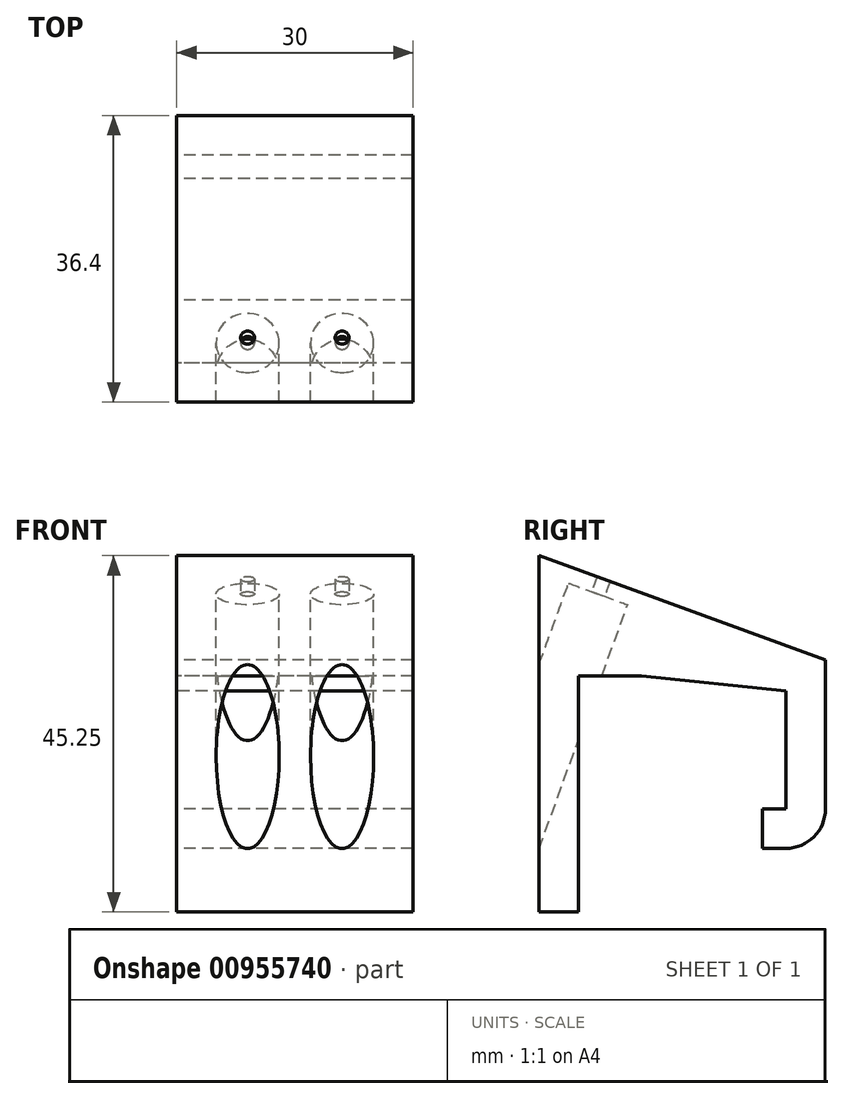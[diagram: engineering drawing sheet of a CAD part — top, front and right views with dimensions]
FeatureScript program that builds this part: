
annotation { "Feature Type Name" : "Feature", "Feature Type Description" : "" }
export const myFeature = defineFeature(function(context is Context, id is Id, definition is map)
    precondition{}
    {
        {
            var Q0;
            Q0=qCreatedBy(makeId("Right.planeOp"),FACE);
            var sketch = newSketch(context, id + "F0", { "sketchPlane" : qUnion([Q0])});
            skLineSegment(sketch, "E0", {"start": v(-5, -30) * mm, "end": v(-5, 15.25) * mm});
            skLineSegment(sketch, "E1", {"start": v(-5, 15.25) * mm, "end": v(31.4, 2) * mm});
            skLineSegment(sketch, "E2", {"start": v(31.4, 2) * mm, "end": v(31.4, -21.93) * mm});
            skLineSegment(sketch, "E3", {"start": v(31.4, -21.93) * mm, "end": v(23.4, -21.93) * mm});
            skLineSegment(sketch, "E4", {"start": v(23.4, -21.93) * mm, "end": v(23.4, -16.93) * mm});
            skLineSegment(sketch, "E5", {"start": v(23.4, -16.93) * mm, "end": v(26.4, -16.93) * mm});
            skLineSegment(sketch, "E6", {"start": v(26.4, -16.93) * mm, "end": v(26.4, -1.93) * mm});
            skLineSegment(sketch, "E7", {"start": v(26.4, -1.93) * mm, "end": v(8, 0) * mm});
            skLineSegment(sketch, "E8", {"start": v(8, 0) * mm, "end": v(0, 0) * mm});
            skLineSegment(sketch, "E9", {"start": v(0, 0) * mm, "end": v(0, -30) * mm});
            skLineSegment(sketch, "E10", {"start": v(0, -30) * mm, "end": v(-5, -30) * mm});
            skSolve(sketch);
        }
        {
            var Q0;
            Q0=makeQuery(id+"F0.imprint","IMPRINT",FACE,{"disambiguationData":[TD([[makeQuery(id+"F0.imprint","IMPRINT",EDGE,{"derivedFrom":sQuery(id+"F0.wireOp",EDGE,"E0")}),-1.0]])]});
            extrude(context, id + "F1", {"entities" : qUnion([Q0]), "depth" : 30 * mm, "offsetDistance" : 25 * mm, "symmetric" : true});
        }
        {
            var Q0;
            Q0=makeQuery(id+"F1.opExtrude","SWEPT_FACE",FACE,{"disambiguationData":[OSD([sQuery(id+"F0.wireOp",EDGE,"E1")])]});
            var sketch = newSketch(context, id + "F2", { "sketchPlane" : qUnion([Q0])});
            skCircle(sketch, "E11", {"center": v(-6, -1.18) * mm, "radius": 4 * mm});
            skCircle(sketch, "E12", {"center": v(6, -1.18) * mm, "radius": 4 * mm});
            skSolve(sketch);
        }
        {
            var Q0;
            Q0=makeQuery(id+"F2.imprint","IMPRINT",FACE,{"disambiguationData":[TD([[makeQuery(id+"F2.imprint","IMPRINT",EDGE,{"derivedFrom":sQuery(id+"F2.wireOp",EDGE,"E11")}),1.0]])]});
            var Q1;
            Q1=makeQuery(id+"F2.imprint","IMPRINT",FACE,{"disambiguationData":[TD([[makeQuery(id+"F2.imprint","IMPRINT",EDGE,{"derivedFrom":sQuery(id+"F2.wireOp",EDGE,"E12")}),1.0]])]});
            var Q2;
            Q2=sQuery(id+"F2.wireOp",EDGE,"E12");
            var Q3;
            Q3=sQuery(id+"F2.wireOp",EDGE,"E11");
            extrude(context, id + "F3", {"entities" : qUnion([Q0, Q1]), "operationType" : NewBodyOperationType.REMOVE, "surfaceEntities" : qUnion([Q2, Q3]), "endBound" : BoundingType.THROUGH_ALL, "oppositeDirection" : true, "depth" : 25 * mm, "offsetDistance" : 25 * mm, "hasSecondDirection" : true, "secondDirectionOppositeDirection" : true, "secondDirectionDepth" : 2 * mm});
        }
        {
            var Q0;
            Q0=sQuery(id+"F2.wireOp",VERTEX,"E12.center");
            var Q1;
            Q1=sQuery(id+"F2.wireOp",VERTEX,"E11.center");
            var Q2;
            Q2=makeQuery(id+"F1.opExtrude","SWEPT_BODY",BODY,{"disambiguationData":[OSD([sQuery(id+"F0.wireOp",EDGE,"E0"),sQuery(id+"F0.wireOp",EDGE,"E1"),sQuery(id+"F0.wireOp",EDGE,"E2"),sQuery(id+"F0.wireOp",EDGE,"E3"),sQuery(id+"F0.wireOp",EDGE,"E4"),sQuery(id+"F0.wireOp",EDGE,"E5"),sQuery(id+"F0.wireOp",EDGE,"E6"),sQuery(id+"F0.wireOp",EDGE,"E7"),sQuery(id+"F0.wireOp",EDGE,"E8"),sQuery(id+"F0.wireOp",EDGE,"E9"),sQuery(id+"F0.wireOp",EDGE,"E10")])]});
            hole(context, id + "F4", {"style" : HoleStyle.SIMPLE, "endStyle" : HoleEndStyle.THROUGH, "standardTappedOrClearance" : lookupTablePath({ "standard" : "ISO", "engagement" : "75%", "pitch" : "0.25 mm", "size" : "M2", "type" : "Tapped" }), "standardBlindInLast" : lookupTablePath({ "standard" : "ISO", "fit" : "Normal", "engagement" : "75%", "pitch" : "0.25 mm", "size" : "M2", "type" : "Clearance & tapped" }), "holeDiameter" : 1.75 * mm, "majorDiameter" : 2 * mm, "showTappedDepth" : true, "isTappedThrough" : true, "tappedDepth" : 12 * mm, "tapClearance" : 3, "locations" : qUnion([Q0, Q1]), "scope" : qUnion([Q2])});
        }
        {
            var Q0;
            Q0=makeQuery(id+"F1.opExtrude","SWEPT_EDGE",EDGE,{"disambiguationData":[OSD([sQuery(id+"F0.wireOp",EDGE,"E2"),sQuery(id+"F0.wireOp",EDGE,"E3")])]});
            fillet(context, id + "F5", {"entities" : qUnion([Q0]), "radius" : 5 * mm, "tangentPropagation" : true, "allowEdgeOverflow" : false});
        }
    });
